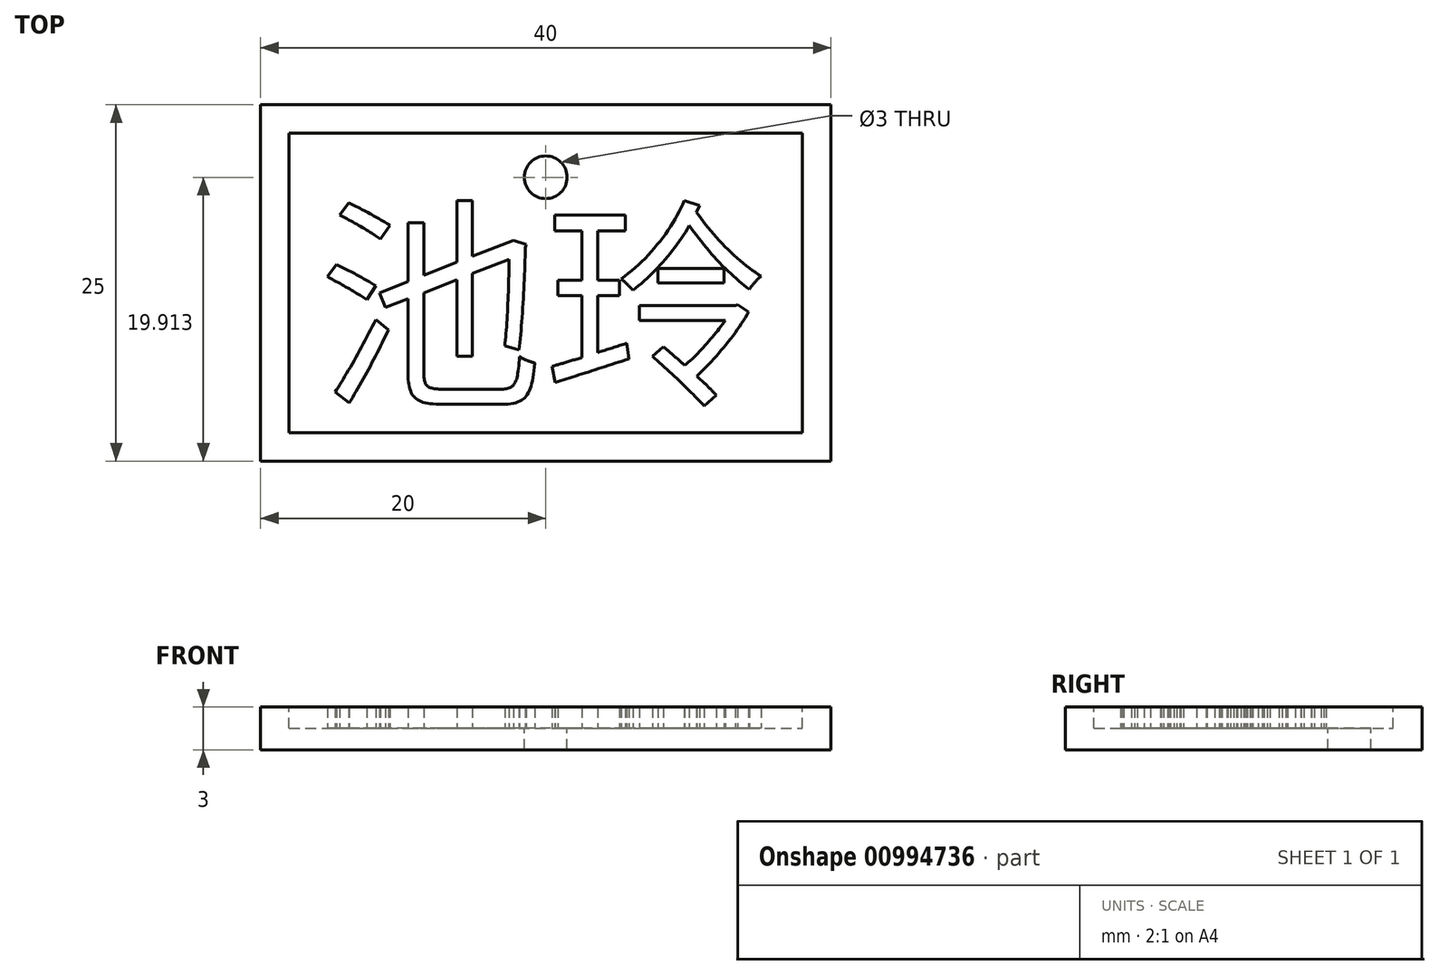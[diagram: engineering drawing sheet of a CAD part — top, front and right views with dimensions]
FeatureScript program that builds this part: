
annotation { "Feature Type Name" : "Feature", "Feature Type Description" : "" }
export const myFeature = defineFeature(function(context is Context, id is Id, definition is map)
    precondition{}
    {
        {
            var Q0;
            Q0=qCreatedBy(makeId("Top.planeOp"),FACE);
            var sketch = newSketch(context, id + "F0", { "sketchPlane" : qUnion([Q0])});
            skLineSegment(sketch, "E0.bottom", {"start": v(20, -12.5) * mm, "end": v(-20, -12.5) * mm});
            skLineSegment(sketch, "E0.top", {"start": v(20, 12.5) * mm, "end": v(-20, 12.5) * mm});
            skLineSegment(sketch, "E0.left", {"start": v(20, -12.5) * mm, "end": v(20, 12.5) * mm});
            skLineSegment(sketch, "E0.right", {"start": v(-20, -12.5) * mm, "end": v(-20, 12.5) * mm});
            skPoint(sketch, "E0.middle", {"position": v(0, 0) * mm});
            skSolve(sketch);
        }
        {
            var Q0;
            Q0 = qSketchRegion(id + "F0", true);
            extrude(context, id + "F1", {"entities" : qUnion([Q0]), "depth" : 3 * mm, "offsetDistance" : 25 * mm});
        }
        {
            var Q0;
            Q0=makeQuery(id+"F1.opExtrude","CAP_FACE",FACE,{"disambiguationData":[OSD([sQuery(id+"F0.wireOp",EDGE,"E0.bottom"),sQuery(id+"F0.wireOp",EDGE,"E0.top"),sQuery(id+"F0.wireOp",EDGE,"E0.left"),sQuery(id+"F0.wireOp",EDGE,"E0.right")])],"isStart":false});
            var sketch = newSketch(context, id + "F2", { "sketchPlane" : qUnion([Q0])});
            skLineSegment(sketch, "E1.0", {"start": v(18, -10.5) * mm, "end": v(18, 10.5) * mm});
            skLineSegment(sketch, "E1.1", {"start": v(-18, -10.5) * mm, "end": v(18, -10.5) * mm});
            skLineSegment(sketch, "E1.2", {"start": v(-18, 10.5) * mm, "end": v(-18, -10.5) * mm});
            skLineSegment(sketch, "E1.3", {"start": v(18, 10.5) * mm, "end": v(-18, 10.5) * mm});
            skSolve(sketch);
        }
        {
            var Q0;
            Q0 = qSketchRegion(id + "F2", true);
            extrude(context, id + "F3", {"entities" : qUnion([Q0]), "operationType" : NewBodyOperationType.REMOVE, "oppositeDirection" : true, "depth" : 1.5 * mm, "offsetDistance" : 25 * mm});
        }
        {
            var Q0;
            Q0=makeQuery(id+"F3.boolean.opBoolean","COPY",FACE,{"derivedFrom":makeQuery(id+"F3.opExtrude","CAP_FACE",FACE,{"disambiguationData":[OSD([sQuery(id+"F2.wireOp",EDGE,"E1.0"),sQuery(id+"F2.wireOp",EDGE,"E1.1"),sQuery(id+"F2.wireOp",EDGE,"E1.2"),sQuery(id+"F2.wireOp",EDGE,"E1.3")])],"isStart":false})});
            var sketch = newSketch(context, id + "F4", { "sketchPlane" : qUnion([Q0])});
            skSolve(sketch);
        }
        {
            var Q0;
            Q0=makeQuery(id+"F4.imprint","IMPRINT",FACE,{"disambiguationData":[TD([[makeQuery(id+"F4.imprint","IMPRINT",EDGE,{"derivedFrom":makeQuery(id+"F3.boolean.opBoolean","COPY",EDGE,{"derivedFrom":makeQuery(id+"F3.opExtrude","CAP_EDGE",EDGE,{"disambiguationData":[OSD([sQuery(id+"F2.wireOp",EDGE,"E1.0")])],"isStart":false})})}),1.0]])]});
            var sketch = newSketch(context, id + "F5", { "sketchPlane" : qUnion([Q0])});
            skCircle(sketch, "E2", {"center": v(0, 7.41) * mm, "radius": 1.5 * mm});
            skSolve(sketch);
        }
        {
            var Q0;
            Q0 = qSketchRegion(id + "F5", true);
            extrude(context, id + "F6", {"entities" : qUnion([Q0]), "operationType" : NewBodyOperationType.REMOVE, "endBound" : BoundingType.THROUGH_ALL, "oppositeDirection" : true, "depth" : 25 * mm, "offsetDistance" : 25 * mm});
        }
        {
            var Q0;
            Q0=makeQuery(id+"F4.imprint","IMPRINT",FACE,{"disambiguationData":[TD([[makeQuery(id+"F4.imprint","IMPRINT",EDGE,{"derivedFrom":makeQuery(id+"F3.boolean.opBoolean","COPY",EDGE,{"derivedFrom":makeQuery(id+"F3.opExtrude","CAP_EDGE",EDGE,{"disambiguationData":[OSD([sQuery(id+"F2.wireOp",EDGE,"E1.0")])],"isStart":false})})}),1.0]])]});
            var sketch = newSketch(context, id + "F7", { "sketchPlane" : qUnion([Q0])});
            skText(sketch, "E3", { "text": "池玲", "fontName": "NotoSansCJKtc-Regular.otf"});
            const initialGuessF7  = {"E3": [-0.016, -0.00745, 1, 0, 0.01142]};
            skSetInitialGuess(sketch, initialGuessF7);
            skSolve(sketch);
        }
        {
            var Q0;
            Q0 = qSketchRegion(id + "F7", true);
            extrude(context, id + "F8", {"entities" : qUnion([Q0]), "operationType" : NewBodyOperationType.ADD, "depth" : 1.5 * mm, "offsetDistance" : 25 * mm});
        }
    });
